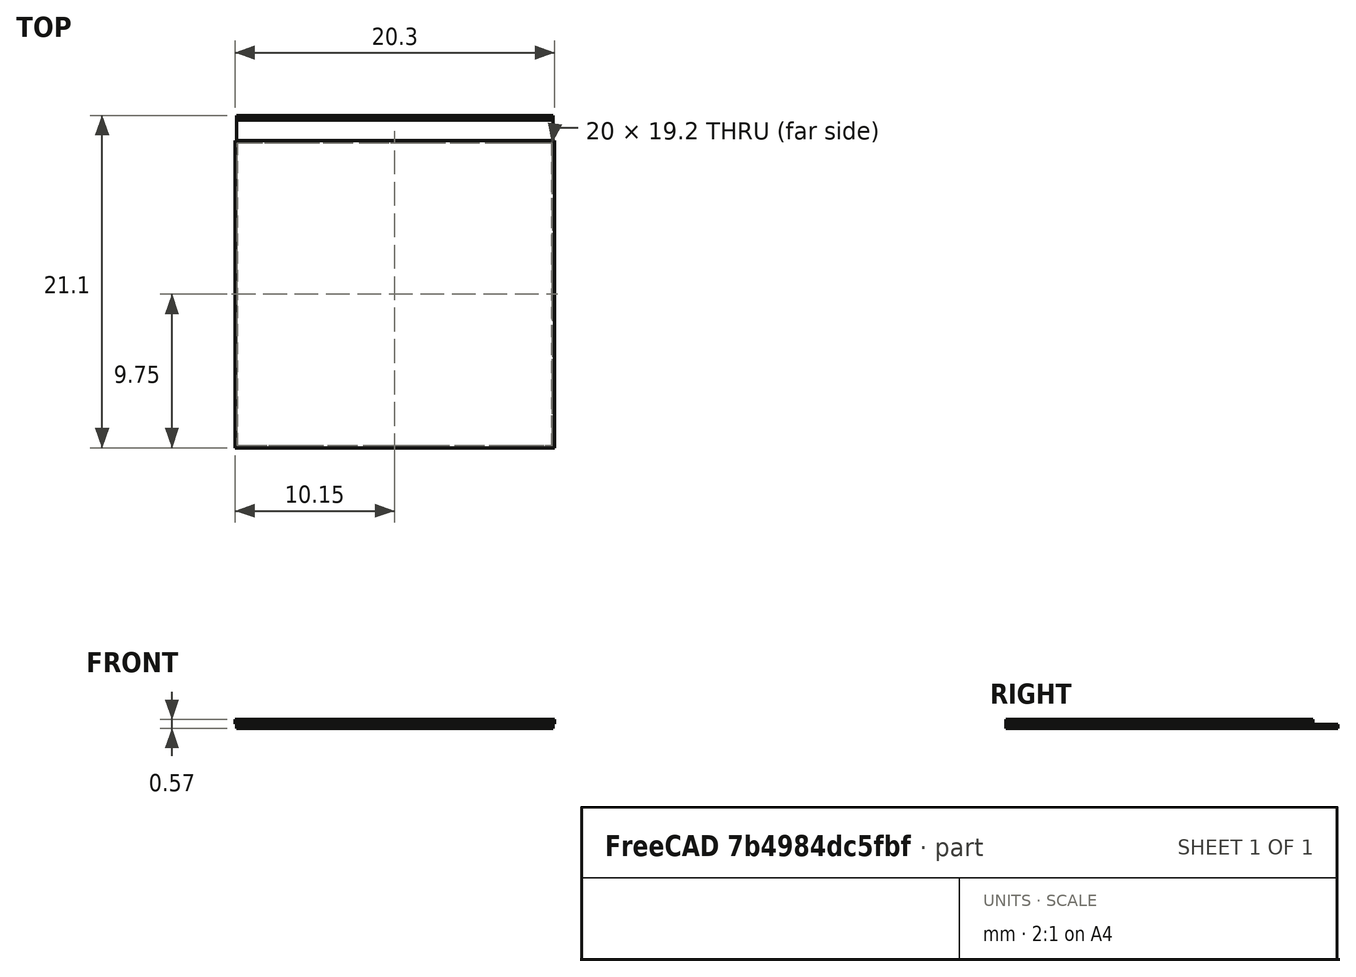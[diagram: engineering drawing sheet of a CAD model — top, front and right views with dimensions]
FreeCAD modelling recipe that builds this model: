
FCSTD DOCUMENT  (FreeCAD 0.17R13541 (Git))
Label: singleHS
License: All rights reserved
LicenseURL: http://en.wikipedia.org/wiki/All_rights_reserved
objects: Sketcher::SketchObject×11, PartDesign::Pad×11, PartDesign::Body×11, PartDesign::ShapeBinder×10, App::MaterialObjectPython×8, Part::FeaturePython×2, Fem::FemSolverObjectPython×1, Fem::ConstraintInitialTemperature×1, Fem::FemMeshObjectPython×1, Fem::FemAnalysis×1
note: 56 computed .brp shape members not serialized (recipe doc carries the construction recipe); baked Part::Feature solids carry a one-line shape summary decoded from their .brp

FEATURE [Sketcher::SketchObject] Sketch
  MapMode = 5
  Support = -> [XY_Plane]
  sketch-geometry (4):
    g0: LineSegment StartX=0 StartY=0 StartZ=0 EndX=20.1 EndY=0 EndZ=0
    g1: LineSegment StartX=20.1 StartY=0 StartZ=0 EndX=20.1 EndY=21.1 EndZ=0
    g2: LineSegment StartX=20.1 StartY=21.1 StartZ=0 EndX=0 EndY=21.1 EndZ=0
    g3: LineSegment StartX=0 StartY=21.1 StartZ=0 EndX=0 EndY=0 EndZ=0
  constraints (11):
    c: Coincident(g0,g1)
    c: Coincident(g1,g2)
    c: Coincident(g2,g3)
    c: Coincident(g3,g0)
    c: Horizontal(g0)
    c: Horizontal(g2)
    c: Vertical(g1)
    c: Vertical(g3)
    c: Coincident(g0,g-1)
    c: DistanceX(g0,g0) = 20.1
    c: DistanceY(g3,g3) = 21.1
FEATURE [PartDesign::Pad] Pad
  Length = 0.15
  Length2 = 100
  Profile = -> Sketch
  Type = 0
FEATURE [PartDesign::Body] Body
  Group = -> [Sketch,Pad]
  Origin = -> Origin
  Tip = -> Pad
FEATURE [PartDesign::ShapeBinder] CopyPad
  Placement = pos=(0,0,0.15) rot=(0,0,1;0rad)
FEATURE [Sketcher::SketchObject] Sketch001
  MapMode = 5
  Placement = pos=(0,0,0.15) rot=(0,0,1;0rad)
  Support = -> [CopyPad]
  sketch-geometry (4):
    g0: LineSegment StartX=0.05 StartY=0.15 StartZ=0 EndX=20.05 EndY=0.15 EndZ=0
    g1: LineSegment StartX=20.05 StartY=0.15 StartZ=0 EndX=20.05 EndY=19.35 EndZ=0
    g2: LineSegment StartX=20.05 StartY=19.35 StartZ=0 EndX=0.05 EndY=19.35 EndZ=0
    g3: LineSegment StartX=0.05 StartY=19.35 StartZ=0 EndX=0.05 EndY=0.15 EndZ=0
  constraints (12):
    c: Coincident(g0,g1)
    c: Coincident(g1,g2)
    c: Coincident(g2,g3)
    c: Coincident(g3,g0)
    c: Horizontal(g0)
    c: Horizontal(g2)
    c: Vertical(g1)
    c: Vertical(g3)
    c: DistanceY(g-1,g0) = 0.15
    c: DistanceX(g-1,g0) = 0.05
    c: DistanceX(g0,g0) = 20
    c: DistanceY(g3,g3) = 19.2
FEATURE [PartDesign::Pad] Pad001
  Length = 0.025
  Length2 = 100
  Placement = pos=(0,0,0.15) rot=(0,0,1;0rad)
  Profile = -> Sketch001
  Type = 0
FEATURE [PartDesign::Body] Body001
  Group = -> [CopyPad,Sketch001,Pad001]
  Origin = -> Origin001
  Tip = -> Pad001
FEATURE [PartDesign::ShapeBinder] CopyPad001
  Placement = pos=(0,0,0.025) rot=(0,0,1;0rad)
FEATURE [Sketcher::SketchObject] Sketch002
  MapMode = 5
  Placement = pos=(0,0,0.175) rot=(0,0,1;0rad)
  Support = -> [CopyPad001]
  sketch-geometry (4):
    g0: LineSegment StartX=-0.1 StartY=0 StartZ=0 EndX=20.2 EndY=0 EndZ=0
    g1: LineSegment StartX=20.2 StartY=0 StartZ=0 EndX=20.2 EndY=19.5 EndZ=0
    g2: LineSegment StartX=20.2 StartY=19.5 StartZ=0 EndX=-0.1 EndY=19.5 EndZ=0
    g3: LineSegment StartX=-0.1 StartY=19.5 StartZ=0 EndX=-0.1 EndY=0 EndZ=0
  constraints (12):
    c: Coincident(g0,g1)
    c: Coincident(g1,g2)
    c: Coincident(g2,g3)
    c: Coincident(g3,g0)
    c: Horizontal(g0)
    c: Horizontal(g2)
    c: Vertical(g1)
    c: Vertical(g3)
    c: DistanceY(g0,g-1) = 0
    c: DistanceX(g0,g-1) = 0.1
    c: DistanceX(g0,g0) = 20.3
    c: DistanceY(g3,g3) = 19.5
FEATURE [PartDesign::Pad] Pad002
  Length = 0.15
  Length2 = 100
  Placement = pos=(0,0,0.025) rot=(0,0,1;0rad)
  Profile = -> Sketch002
  Type = 0
FEATURE [PartDesign::Body] Body002
  Group = -> [CopyPad001,Sketch002,Pad002]
  Origin = -> Origin002
  Tip = -> Pad002
FEATURE [PartDesign::ShapeBinder] CopyPad002
  Placement = pos=(0,0,0.15) rot=(0,0,1;0rad)
FEATURE [Sketcher::SketchObject] Sketch003
  MapMode = 5
  Placement = pos=(0,0,0.325) rot=(0,0,1;0rad)
  Support = -> [CopyPad002]
  sketch-geometry (4):
    g0: LineSegment StartX=-0.1 StartY=0 StartZ=0 EndX=20.2 EndY=0 EndZ=0
    g1: LineSegment StartX=20.2 StartY=0 StartZ=0 EndX=20.2 EndY=19.5 EndZ=0
    g2: LineSegment StartX=20.2 StartY=19.5 StartZ=0 EndX=-0.1 EndY=19.5 EndZ=0
    g3: LineSegment StartX=-0.1 StartY=19.5 StartZ=0 EndX=-0.1 EndY=0 EndZ=0
  constraints (12):
    c: Coincident(g0,g1)
    c: Coincident(g1,g2)
    c: Coincident(g2,g3)
    c: Coincident(g3,g0)
    c: Horizontal(g0)
    c: Horizontal(g2)
    c: Vertical(g1)
    c: Vertical(g3)
    c: DistanceY(g0,g-1) = 0
    c: DistanceX(g0,g-1) = 0.1
    c: DistanceX(g0,g0) = 20.3
    c: DistanceY(g3,g3) = 19.5
FEATURE [PartDesign::Pad] Pad003
  Length = 0.05
  Length2 = 100
  Placement = pos=(0,0,0.15) rot=(0,0,1;0rad)
  Profile = -> Sketch003
  Type = 0
FEATURE [PartDesign::Body] Body003
  Group = -> [CopyPad002,Sketch003,Pad003]
  Origin = -> Origin003
  Tip = -> Pad003
FEATURE [PartDesign::ShapeBinder] CopyPad003
  Placement = pos=(0,0,0.05) rot=(0,0,1;0rad)
FEATURE [Sketcher::SketchObject] Sketch004
  MapMode = 5
  Placement = pos=(0,0,0.375) rot=(0,0,1;0rad)
  Support = -> [CopyPad003]
  sketch-geometry (4):
    g0: LineSegment StartX=-0.1 StartY=0 StartZ=0 EndX=20.2 EndY=0 EndZ=0
    g1: LineSegment StartX=20.2 StartY=0 StartZ=0 EndX=20.2 EndY=19.5 EndZ=0
    g2: LineSegment StartX=20.2 StartY=19.5 StartZ=0 EndX=-0.1 EndY=19.5 EndZ=0
    g3: LineSegment StartX=-0.1 StartY=19.5 StartZ=0 EndX=-0.1 EndY=0 EndZ=0
  constraints (12):
    c: Coincident(g0,g1)
    c: Coincident(g1,g2)
    c: Coincident(g2,g3)
    c: Coincident(g3,g0)
    c: Horizontal(g0)
    c: Horizontal(g2)
    c: Vertical(g1)
    c: Vertical(g3)
    c: DistanceX(g0,g-1) = 0.1
    c: DistanceY(g0,g-1) = 0
    c: DistanceX(g0,g0) = 20.3
    c: DistanceY(g3,g3) = 19.5
FEATURE [PartDesign::Pad] Pad004
  Length = 0.0225
  Length2 = 100
  Placement = pos=(0,0,0.05) rot=(0,0,1;0rad)
  Profile = -> Sketch004
  Type = 0
FEATURE [PartDesign::Body] Body004
  Group = -> [CopyPad003,Sketch004,Pad004]
  Origin = -> Origin004
  Tip = -> Pad004
FEATURE [PartDesign::ShapeBinder] CopyPad004
  Placement = pos=(0,0,0.0225) rot=(0,0,1;0rad)
FEATURE [Sketcher::SketchObject] Sketch005
  MapMode = 5
  Placement = pos=(0,0,0.3975) rot=(0,0,1;0rad)
  Support = -> [CopyPad004]
  sketch-geometry (4):
    g0: LineSegment StartX=-0.1 StartY=0 StartZ=0 EndX=20.2 EndY=0 EndZ=0
    g1: LineSegment StartX=20.2 StartY=0 StartZ=0 EndX=20.2 EndY=19.5 EndZ=0
    g2: LineSegment StartX=20.2 StartY=19.5 StartZ=0 EndX=-0.1 EndY=19.5 EndZ=0
    g3: LineSegment StartX=-0.1 StartY=19.5 StartZ=0 EndX=-0.1 EndY=0 EndZ=0
  constraints (12):
    c: Coincident(g0,g1)
    c: Coincident(g1,g2)
    c: Coincident(g2,g3)
    c: Coincident(g3,g0)
    c: Horizontal(g0)
    c: Horizontal(g2)
    c: Vertical(g1)
    c: Vertical(g3)
    c: DistanceY(g0,g-1) = 0
    c: DistanceX(g0,g-1) = 0.1
    c: DistanceX(g0,g0) = 20.3
    c: DistanceY(g3,g3) = 19.5
FEATURE [PartDesign::Pad] Pad005
  Length = 0.0175
  Length2 = 100
  Placement = pos=(0,0,0.0225) rot=(0,0,1;0rad)
  Profile = -> Sketch005
  Type = 0
FEATURE [PartDesign::Body] Body005
  Group = -> [CopyPad004,Sketch005,Pad005]
  Origin = -> Origin005
  Tip = -> Pad005
FEATURE [PartDesign::ShapeBinder] CopyPad005
  Placement = pos=(0,0,0.0175) rot=(0,0,1;0rad)
FEATURE [Sketcher::SketchObject] Sketch006
  MapMode = 5
  Placement = pos=(0,0,0.415) rot=(0,0,1;0rad)
  Support = -> [CopyPad005]
  sketch-geometry (4):
    g0: LineSegment StartX=-0.1 StartY=0 StartZ=0 EndX=20.2 EndY=0 EndZ=0
    g1: LineSegment StartX=20.2 StartY=0 StartZ=0 EndX=20.2 EndY=19.5 EndZ=0
    g2: LineSegment StartX=20.2 StartY=19.5 StartZ=0 EndX=-0.1 EndY=19.5 EndZ=0
    g3: LineSegment StartX=-0.1 StartY=19.5 StartZ=0 EndX=-0.1 EndY=0 EndZ=0
  constraints (12):
    c: Coincident(g0,g1)
    c: Coincident(g1,g2)
    c: Coincident(g2,g3)
    c: Coincident(g3,g0)
    c: Horizontal(g0)
    c: Horizontal(g2)
    c: Vertical(g1)
    c: Vertical(g3)
    c: DistanceY(g0,g-1) = 0
    c: DistanceX(g0,g-1) = 0.1
    c: DistanceX(g0,g0) = 20.3
    c: DistanceY(g3,g3) = 19.5
FEATURE [PartDesign::Pad] Pad006
  Length = 0.02
  Length2 = 100
  Placement = pos=(0,0,0.0175) rot=(0,0,1;0rad)
  Profile = -> Sketch006
  Type = 0
FEATURE [PartDesign::Body] Body006
  Group = -> [CopyPad005,Sketch006,Pad006]
  Origin = -> Origin006
  Tip = -> Pad006
FEATURE [PartDesign::ShapeBinder] CopyPad006
  Placement = pos=(0,0,0.02) rot=(0,0,1;0rad)
FEATURE [Sketcher::SketchObject] Sketch007
  MapMode = 5
  Placement = pos=(0,0,0.435) rot=(0,0,1;0rad)
  Support = -> [CopyPad006]
  sketch-geometry (4):
    g0: LineSegment StartX=-0.1 StartY=0 StartZ=0 EndX=20.2 EndY=0 EndZ=0
    g1: LineSegment StartX=20.2 StartY=0 StartZ=0 EndX=20.2 EndY=19.5 EndZ=0
    g2: LineSegment StartX=20.2 StartY=19.5 StartZ=0 EndX=-0.1 EndY=19.5 EndZ=0
    g3: LineSegment StartX=-0.1 StartY=19.5 StartZ=0 EndX=-0.1 EndY=0 EndZ=0
  constraints (12):
    c: Coincident(g0,g1)
    c: Coincident(g1,g2)
    c: Coincident(g2,g3)
    c: Coincident(g3,g0)
    c: Horizontal(g0)
    c: Horizontal(g2)
    c: Vertical(g1)
    c: Vertical(g3)
    c: DistanceY(g0,g-1) = 0
    c: DistanceX(g0,g-1) = 0.1
    c: DistanceX(g0,g0) = 20.3
    c: DistanceY(g3,g3) = 19.5
FEATURE [PartDesign::Pad] Pad007
  Length = 0.0175
  Length2 = 100
  Placement = pos=(0,0,0.02) rot=(0,0,1;0rad)
  Profile = -> Sketch007
  Type = 0
FEATURE [PartDesign::Body] Body007
  Group = -> [CopyPad006,Sketch007,Pad007]
  Origin = -> Origin007
  Tip = -> Pad007
FEATURE [PartDesign::ShapeBinder] CopyPad007
  Placement = pos=(0,0,0.0175) rot=(0,0,1;0rad)
FEATURE [Sketcher::SketchObject] Sketch008
  MapMode = 5
  Placement = pos=(0,0,0.4525) rot=(0,0,1;0rad)
  Support = -> [CopyPad007]
  sketch-geometry (4):
    g0: LineSegment StartX=-0.1 StartY=0 StartZ=0 EndX=20.2 EndY=0 EndZ=0
    g1: LineSegment StartX=20.2 StartY=0 StartZ=0 EndX=20.2 EndY=19.5 EndZ=0
    g2: LineSegment StartX=20.2 StartY=19.5 StartZ=0 EndX=-0.1 EndY=19.5 EndZ=0
    g3: LineSegment StartX=-0.1 StartY=19.5 StartZ=0 EndX=-0.1 EndY=0 EndZ=0
  constraints (12):
    c: Coincident(g0,g1)
    c: Coincident(g1,g2)
    c: Coincident(g2,g3)
    c: Coincident(g3,g0)
    c: Horizontal(g0)
    c: Horizontal(g2)
    c: Vertical(g1)
    c: Vertical(g3)
    c: DistanceY(g0,g-1) = 0
    c: DistanceX(g0,g-1) = 0.1
    c: DistanceX(g0,g0) = 20.3
    c: DistanceY(g3,g3) = 19.5
FEATURE [PartDesign::Pad] Pad008
  Length = 0.0225
  Length2 = 100
  Placement = pos=(0,0,0.0175) rot=(0,0,1;0rad)
  Profile = -> Sketch008
  Type = 0
FEATURE [PartDesign::Body] Body008
  Group = -> [CopyPad007,Sketch008,Pad008]
  Origin = -> Origin008
  Tip = -> Pad008
FEATURE [PartDesign::ShapeBinder] CopyPad008
FEATURE [Sketcher::SketchObject] Sketch009
  MapMode = 5
  Placement = pos=(0,0,0) rot=(1,0,0;3.14159rad)
  Support = -> [CopyPad008]
  sketch-geometry (4):
    g0: LineSegment StartX=0 StartY=0 StartZ=0 EndX=20.1 EndY=0 EndZ=0
    g1: LineSegment StartX=20.1 StartY=0 StartZ=0 EndX=20.1 EndY=-21.1 EndZ=0
    g2: LineSegment StartX=20.1 StartY=-21.1 StartZ=0 EndX=0 EndY=-21.1 EndZ=0
    g3: LineSegment StartX=0 StartY=-21.1 StartZ=0 EndX=0 EndY=0 EndZ=0
  constraints (11):
    c: Coincident(g0,g1)
    c: Coincident(g1,g2)
    c: Coincident(g2,g3)
    c: Coincident(g3,g0)
    c: Horizontal(g0)
    c: Horizontal(g2)
    c: Vertical(g1)
    c: Vertical(g3)
    c: Coincident(g0,g-1)
    c: DistanceX(g2,g2) = 20.1
    c: DistanceY(g3,g3) = 21.1
FEATURE [PartDesign::Pad] Pad009
  Length = 0.1
  Length2 = 100
  Profile = -> Sketch009
  Type = 0
FEATURE [PartDesign::Body] Body009
  Group = -> [CopyPad008,Sketch009,Pad009]
  Origin = -> Origin009
  Tip = -> Pad009
FEATURE [PartDesign::ShapeBinder] CopyPad009
  Placement = pos=(0,0,0.15) rot=(0,0,1;0rad)
FEATURE [Sketcher::SketchObject] Sketch010
  ExternalGeometry = -> [CopyPad009]
  MapMode = 5
  Placement = pos=(0,0,0.15) rot=(0,0,1;0rad)
  Support = -> [CopyPad009]
  sketch-geometry (4):
    g0: LineSegment StartX=0 StartY=21 StartZ=0 EndX=20.1 EndY=21 EndZ=0
    g1: LineSegment StartX=20.1 StartY=21 StartZ=0 EndX=20.1 EndY=20.83 EndZ=0
    g2: LineSegment StartX=20.1 StartY=20.83 StartZ=0 EndX=0 EndY=20.83 EndZ=0
    g3: LineSegment StartX=0 StartY=20.83 StartZ=0 EndX=0 EndY=21 EndZ=0
  constraints (12):
    c: Coincident(g0,g1)
    c: Coincident(g1,g2)
    c: Coincident(g2,g3)
    c: Coincident(g3,g0)
    c: Horizontal(g0)
    c: Horizontal(g2)
    c: Vertical(g1)
    c: Vertical(g3)
    c: DistanceX(g0,g-3) = 0
    c: DistanceY(g0,g-3) = 0.1
    c: DistanceY(g1,g1) = 0.17
    c: DistanceX(g2,g2) = 20.1
FEATURE [Fem::FemSolverObjectPython] CalculiXccxTools  # FEM object (typed FeaturePython)
  AnalysisType = 2
  BeamShellResultOutput3D = false
  EigenmodeHighLimit = 1000000
  EigenmodeLowLimit = 0
  EigenmodesCount = 10
  GeometricalNonlinearity = 0
  IterationsControlParameterCutb = 0.25,0.5,0.75,0.85,,,1.5,
  IterationsControlParameterIter = 4,8,9,200,10,400,,200,,
  IterationsControlParameterTimeUse = false
  IterationsThermoMechMaximum = 2000
  IterationsUserDefinedIncrementations = false
  IterationsUserDefinedTimeStepLength = false
  MaterialNonlinearity = 0
  MatrixSolverType = 0
  SplitInputWriter = false
  ThermoMechSteadyState = true
  TimeEnd = 1
  TimeInitialStep = 0.01
FEATURE [Fem::ConstraintInitialTemperature] FemConstraintInitialTemperature
  NormalDirection = (0,0,1)
  initialTemperature = 300
FEATURE [App::MaterialObjectPython] SolidMaterial  # material (typed FeaturePython)
  Category = 0
  Material = Density=2.356e+12 kg/m^3; Description=This is a not defined material; Father=None; Name=None; PoissonRatio=0.35; SpecificHeat=0.8 J/kg/K; SpecificPrice=0; ThermalConductivity=1.26 W/m/K; ThermalExpansionCoefficient=85.0 um/m/K; UltimateTensileStrength=0 MPa; YoungsModulus=1900000.0 kPa
  References = -> [Pad009]
FEATURE [App::MaterialObjectPython] SolidMaterial001  # material (typed FeaturePython)
  Category = 0
  Material = Density=2329.0 kg/m^3; Description=This is a not defined material; Father=None; Name=None; PoissonRatio=0.28; SpecificHeat=0.71 J/kg/K; SpecificPrice=0; ThermalConductivity=124.0 W/m/K; ThermalExpansionCoefficient=2.0 um/m/K; UltimateTensileStrength=0 MPa; YoungsModulus=188000000.0 kPa
  References = -> [Pad]
FEATURE [App::MaterialObjectPython] SolidMaterial002  # material (typed FeaturePython)
  Category = 0
  Material = Density=1500.0 kg/m^3; Description=This is a not defined material; Father=None; Name=None; PoissonRatio=0.34; SpecificHeat=0.21 J/kg/K; SpecificPrice=0; ThermalConductivity=63.2 W/m/K; ThermalExpansionCoefficient=21.0 um/m/K; UltimateTensileStrength=0 MPa; YoungsModulus=10000000.0 kPa
  References = -> [Pad001]
FEATURE [App::MaterialObjectPython] SolidMaterial003  # material (typed FeaturePython)
  Category = 0
  Material = Density=2329.0 kg/m^3; Description=This is a not defined material; Father=None; Name=None; PoissonRatio=0.28; SpecificHeat=0.71 J/kg/K; SpecificPrice=0; ThermalConductivity=124.0 W/m/K; ThermalExpansionCoefficient=2.0 um/m/K; UltimateTensileStrength=0 MPa; YoungsModulus=188000000.0 kPa
  References = -> [Pad002]
FEATURE [App::MaterialObjectPython] SolidMaterial004  # material (typed FeaturePython)
  Category = 0
  Material = Density=1000.0 kg/m^3; Description=This is a not defined material; Father=None; Name=None; PoissonRatio=0.35; SpecificHeat=0.8 J/kg/K; SpecificPrice=0; ThermalConductivity=0.22 W/m/K; ThermalExpansionCoefficient=85.0 um/m/K; UltimateTensileStrength=0 MPa; YoungsModulus=1900000.0 kPa
  References = -> [Pad003]
FEATURE [App::MaterialObjectPython] SolidMaterial005  # material (typed FeaturePython)
  Category = 0
  Material = Density=142.0 kg/m^3; Description=This is a not defined material; Father=None; Name=None; PoissonRatio=0.34; SpecificHeat=1.09 J/kg/K; SpecificPrice=0; ThermalConductivity=0.12 W/m/K; ThermalExpansionCoefficient=20.0 um/m/K; UltimateTensileStrength=0 MPa; YoungsModulus=4000000.0 kPa
  References = -> [Pad004,Pad006,Pad008]
FEATURE [App::MaterialObjectPython] SolidMaterial006  # material (typed FeaturePython)
  Category = 0
  Material = Density=7764.0 kg/m^3; Description=This is a not defined material; Father=None; Name=None; PoissonRatio=0.343; SpecificHeat=0.385 J/kg/K; SpecificPrice=0; ThermalConductivity=400.0 W/m/K; ThermalExpansionCoefficient=16.4 um/m/K; UltimateTensileStrength=0 MPa; YoungsModulus=110000000.0 kPa
  References = -> [Pad005]
FEATURE [App::MaterialObjectPython] SolidMaterial007  # material (typed FeaturePython)
  Category = 0
  Material = Density=2809.7 kg/m^3; Description=This is a not defined material; Father=None; Name=None; PoissonRatio=0.341; SpecificHeat=0.8433 J/kg/K; SpecificPrice=0; ThermalConductivity=140.08 W/m/K; ThermalExpansionCoefficient=18.74 um/m/K; UltimateTensileStrength=0 MPa; YoungsModulus=41100000.0 kPa
  References = -> [Pad007]
FEATURE [PartDesign::Pad] Pad010
  Length = 0.15
  Length2 = 100
  Placement = pos=(0,0,0.15) rot=(0,0,1;0rad)
  Profile = -> Sketch010
  Reversed = true
  Type = 0
FEATURE [PartDesign::Body] Body010
  Group = -> [CopyPad009,Sketch010,Pad010]
  Origin = -> Origin010
  Tip = -> Pad010
FEATURE [Part::FeaturePython] BooleanFragments  # WARN: FeaturePython — macro-defined, semantics opaque (R4)
  Mode = 2
  Objects = -> [Body010,Body,Body001,Body002,Body004,Body003,Body005,Body007,Body006,Body008,Body009]
  Tolerance = 0
FEATURE [Part::FeaturePython] CompoundFilter  # WARN: FeaturePython — macro-defined, semantics opaque (R4)
  Base = -> BooleanFragments
  FilterType = 3
  Invert = false
  OverrideMaxVal = 0
  WindowFrom = 80
  WindowTo = 100
FEATURE [Fem::FemMeshObjectPython] FEMMeshGmsh  # FEM object (typed FeaturePython)
  Algorithm2D = 0
  Algorithm3D = 0
  CharacteristicLengthMax = 2
  CharacteristicLengthMin = 0
  CoherenceMesh = true
  ElementDimension = 0
  ElementOrder = 1
  GeometryTolerance = 1e-06
  GroupsOfNodes = false
  HighOrderOptimize = false
  OptimizeNetgen = false
  OptimizeStd = true
  Part = -> CompoundFilter
  RecombineAll = false
FEATURE [Fem::FemAnalysis] Analysis
  Group = -> [CalculiXccxTools,FemConstraintInitialTemperature,SolidMaterial,SolidMaterial001,SolidMaterial002,SolidMaterial003,SolidMaterial004,SolidMaterial005,SolidMaterial006,SolidMaterial007,FEMMeshGmsh]
